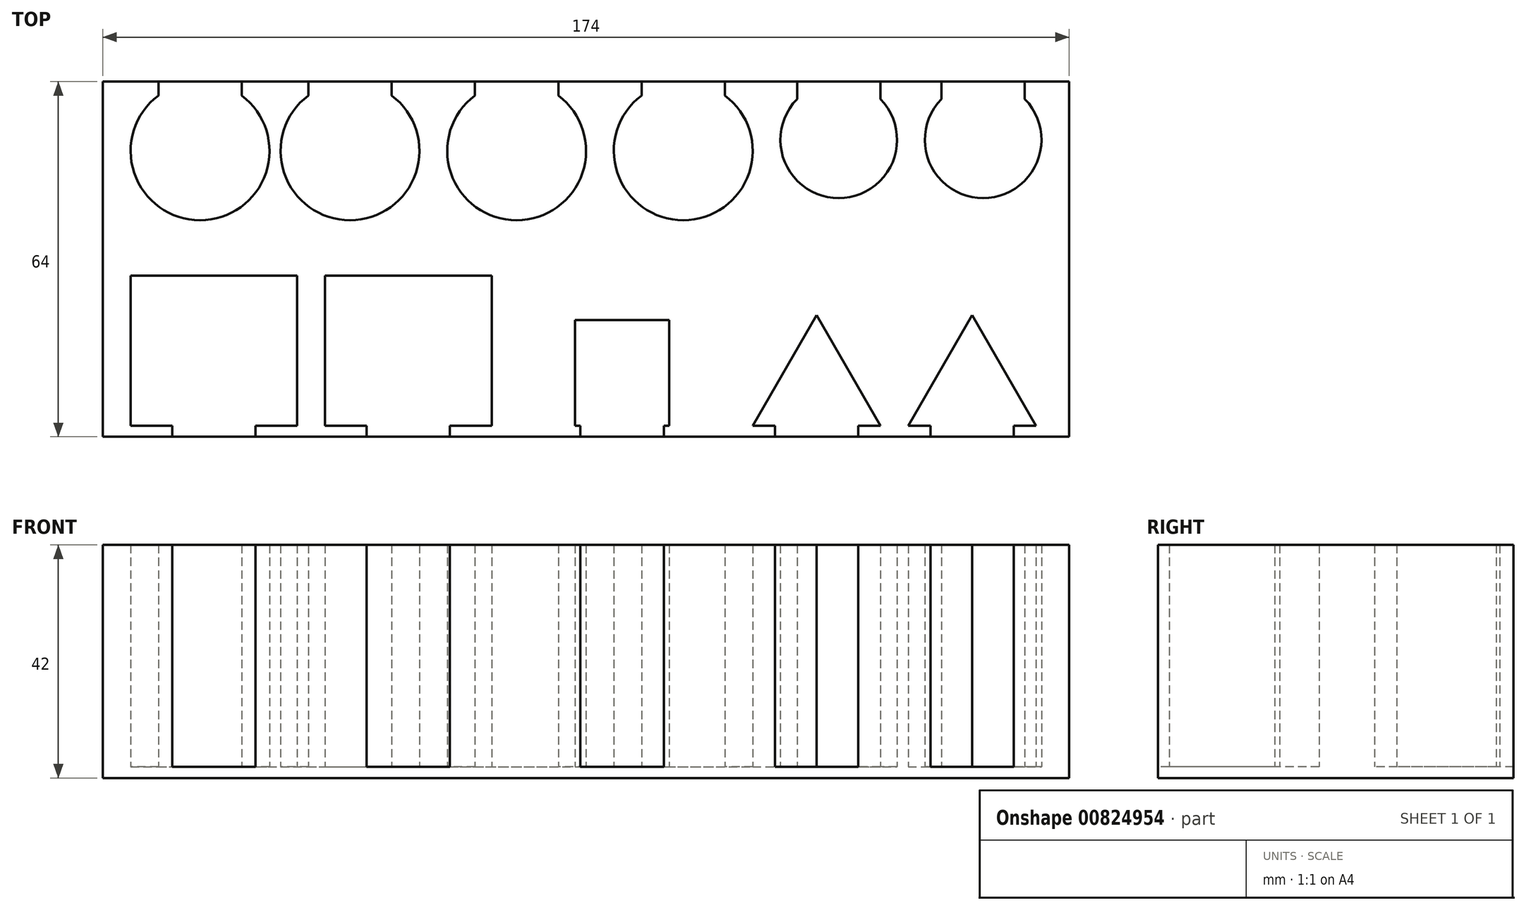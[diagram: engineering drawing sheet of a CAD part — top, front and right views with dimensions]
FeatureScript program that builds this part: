
annotation { "Feature Type Name" : "Feature", "Feature Type Description" : "" }
export const myFeature = defineFeature(function(context is Context, id is Id, definition is map)
    precondition{}
    {
        {
            var Q0;
            Q0=qCreatedBy(makeId("Top.planeOp"),FACE);
            var sketch = newSketch(context, id + "F0", { "sketchPlane" : qUnion([Q0])});
            skLineSegment(sketch, "E0.bottom", {"start": v(0, 0) * mm, "end": v(174, 0) * mm});
            skLineSegment(sketch, "E0.top", {"start": v(0, 64) * mm, "end": v(174, 64) * mm});
            skLineSegment(sketch, "E0.left", {"start": v(0, 0) * mm, "end": v(0, 64) * mm});
            skLineSegment(sketch, "E0.right", {"start": v(174, 0) * mm, "end": v(174, 64) * mm});
            skLineSegment(sketch, "E1.bottom", {"start": v(5, 29) * mm, "end": v(35, 29) * mm});
            skLineSegment(sketch, "E1.top", {"start": v(5, 2) * mm, "end": v(35, 2) * mm});
            skLineSegment(sketch, "E1.left", {"start": v(5, 29) * mm, "end": v(5, 2) * mm});
            skLineSegment(sketch, "E1.right", {"start": v(35, 29) * mm, "end": v(35, 2) * mm});
            skLineSegment(sketch, "E2.bottom", {"start": v(40, 29) * mm, "end": v(70, 29) * mm});
            skLineSegment(sketch, "E2.top", {"start": v(40, 2) * mm, "end": v(70, 2) * mm});
            skLineSegment(sketch, "E2.left", {"start": v(40, 29) * mm, "end": v(40, 2) * mm});
            skLineSegment(sketch, "E2.right", {"start": v(70, 29) * mm, "end": v(70, 2) * mm});
            skLineSegment(sketch, "E3.bottom", {"start": v(85, 21) * mm, "end": v(102, 21) * mm});
            skLineSegment(sketch, "E3.top", {"start": v(85, 2) * mm, "end": v(102, 2) * mm});
            skLineSegment(sketch, "E3.left", {"start": v(85, 21) * mm, "end": v(85, 2) * mm});
            skLineSegment(sketch, "E3.right", {"start": v(102, 21) * mm, "end": v(102, 2) * mm});
            skLineSegment(sketch, "E4", {"start": v(128.5, 21.92) * mm, "end": v(117, 2) * mm});
            skLineSegment(sketch, "E5", {"start": v(117, 2) * mm, "end": v(140, 2) * mm});
            skLineSegment(sketch, "E6", {"start": v(140, 2) * mm, "end": v(128.5, 21.92) * mm});
            skLineSegment(sketch, "E7", {"start": v(156.5, 21.92) * mm, "end": v(145, 2) * mm});
            skLineSegment(sketch, "E8", {"start": v(145, 2) * mm, "end": v(168, 2) * mm});
            skLineSegment(sketch, "E9", {"start": v(168, 2) * mm, "end": v(156.5, 21.92) * mm});
            skCircle(sketch, "E10", {"center": v(74.5, 51.5) * mm, "radius": 12.5 * mm});
            skCircle(sketch, "E11", {"center": v(104.5, 51.5) * mm, "radius": 12.5 * mm});
            skLineSegment(sketch, "E12", {"start": v(74.5, 51.5) * mm, "end": v(104.5, 51.5) * mm, "construction": true});
            skCircle(sketch, "E13", {"center": v(132.5, 53.5) * mm, "radius": 10.5 * mm});
            skCircle(sketch, "E14", {"center": v(158.5, 53.5) * mm, "radius": 10.5 * mm});
            skLineSegment(sketch, "E15", {"start": v(132.5, 53.5) * mm, "end": v(158.5, 53.5) * mm, "construction": true});
            skCircle(sketch, "E16", {"center": v(17.5, 51.5) * mm, "radius": 12.5 * mm});
            skCircle(sketch, "E17", {"center": v(44.5, 51.5) * mm, "radius": 12.5 * mm});
            skLineSegment(sketch, "E18", {"start": v(17.5, 51.5) * mm, "end": v(44.5, 51.5) * mm, "construction": true});
            skLineSegment(sketch, "E19.bottom", {"start": v(117, 51.5) * mm, "end": v(122, 51.5) * mm, "construction": true});
            skLineSegment(sketch, "E19.top", {"start": v(117, 41.5) * mm, "end": v(122, 41.5) * mm, "construction": true});
            skLineSegment(sketch, "E19.left", {"start": v(117, 51.5) * mm, "end": v(117, 41.5) * mm, "construction": true});
            skLineSegment(sketch, "E19.right", {"start": v(122, 51.5) * mm, "end": v(122, 41.5) * mm, "construction": true});
            skLineSegment(sketch, "E20.bottom", {"start": v(10, 64) * mm, "end": v(25, 64) * mm});
            skLineSegment(sketch, "E20.top", {"start": v(10, 51.5) * mm, "end": v(25, 51.5) * mm});
            skLineSegment(sketch, "E20.left", {"start": v(10, 64) * mm, "end": v(10, 51.5) * mm});
            skLineSegment(sketch, "E20.right", {"start": v(25, 64) * mm, "end": v(25, 51.5) * mm});
            skLineSegment(sketch, "E21.bottom", {"start": v(37, 64) * mm, "end": v(52, 64) * mm});
            skLineSegment(sketch, "E21.top", {"start": v(37, 51.5) * mm, "end": v(52, 51.5) * mm});
            skLineSegment(sketch, "E21.left", {"start": v(37, 64) * mm, "end": v(37, 51.5) * mm});
            skLineSegment(sketch, "E21.right", {"start": v(52, 64) * mm, "end": v(52, 51.5) * mm});
            skLineSegment(sketch, "E22.bottom", {"start": v(67, 64) * mm, "end": v(82, 64) * mm});
            skLineSegment(sketch, "E22.top", {"start": v(67, 51.5) * mm, "end": v(82, 51.5) * mm});
            skLineSegment(sketch, "E22.left", {"start": v(67, 64) * mm, "end": v(67, 51.5) * mm});
            skLineSegment(sketch, "E22.right", {"start": v(82, 64) * mm, "end": v(82, 51.5) * mm});
            skLineSegment(sketch, "E23.bottom", {"start": v(97, 64) * mm, "end": v(112, 64) * mm});
            skLineSegment(sketch, "E23.top", {"start": v(97, 51.5) * mm, "end": v(112, 51.5) * mm});
            skLineSegment(sketch, "E23.left", {"start": v(97, 64) * mm, "end": v(97, 51.5) * mm});
            skLineSegment(sketch, "E23.right", {"start": v(112, 64) * mm, "end": v(112, 51.5) * mm});
            skLineSegment(sketch, "E24.bottom", {"start": v(125, 64) * mm, "end": v(140, 64) * mm});
            skLineSegment(sketch, "E24.top", {"start": v(125, 53.5) * mm, "end": v(140, 53.5) * mm});
            skLineSegment(sketch, "E24.left", {"start": v(125, 64) * mm, "end": v(125, 53.5) * mm});
            skLineSegment(sketch, "E24.right", {"start": v(140, 64) * mm, "end": v(140, 53.5) * mm});
            skLineSegment(sketch, "E25.bottom", {"start": v(151, 64) * mm, "end": v(166, 64) * mm});
            skLineSegment(sketch, "E25.top", {"start": v(151, 53.5) * mm, "end": v(166, 53.5) * mm});
            skLineSegment(sketch, "E25.left", {"start": v(151, 64) * mm, "end": v(151, 53.5) * mm});
            skLineSegment(sketch, "E25.right", {"start": v(166, 64) * mm, "end": v(166, 53.5) * mm});
            skLineSegment(sketch, "E26.bottom", {"start": v(121, 8.93) * mm, "end": v(136, 8.93) * mm});
            skLineSegment(sketch, "E26.top", {"start": v(121, 0) * mm, "end": v(136, 0) * mm});
            skLineSegment(sketch, "E26.left", {"start": v(121, 8.93) * mm, "end": v(121, 0) * mm});
            skLineSegment(sketch, "E26.right", {"start": v(136, 8.93) * mm, "end": v(136, 0) * mm});
            skLineSegment(sketch, "E27.bottom", {"start": v(149, 8.93) * mm, "end": v(164, 8.93) * mm});
            skLineSegment(sketch, "E27.top", {"start": v(149, 0) * mm, "end": v(164, 0) * mm});
            skLineSegment(sketch, "E27.left", {"start": v(149, 8.93) * mm, "end": v(149, 0) * mm});
            skLineSegment(sketch, "E27.right", {"start": v(164, 8.93) * mm, "end": v(164, 0) * mm});
            skLineSegment(sketch, "E28.bottom", {"start": v(86, 2) * mm, "end": v(101, 2) * mm});
            skLineSegment(sketch, "E28.top", {"start": v(86, 0) * mm, "end": v(101, 0) * mm});
            skLineSegment(sketch, "E28.left", {"start": v(86, 2) * mm, "end": v(86, 0) * mm});
            skLineSegment(sketch, "E28.right", {"start": v(101, 2) * mm, "end": v(101, 0) * mm});
            skPoint(sketch, "E29", {"position": v(93.5, 2) * mm});
            skPoint(sketch, "E30", {"position": v(55, 2) * mm});
            skPoint(sketch, "E31", {"position": v(20, 2) * mm});
            skLineSegment(sketch, "E32.bottom", {"start": v(12.5, 2) * mm, "end": v(27.5, 2) * mm});
            skLineSegment(sketch, "E32.top", {"start": v(12.5, 0) * mm, "end": v(27.5, 0) * mm});
            skLineSegment(sketch, "E32.left", {"start": v(12.5, 2) * mm, "end": v(12.5, 0) * mm});
            skLineSegment(sketch, "E32.right", {"start": v(27.5, 2) * mm, "end": v(27.5, 0) * mm});
            skLineSegment(sketch, "E33.bottom", {"start": v(47.5, 2) * mm, "end": v(62.5, 2) * mm});
            skLineSegment(sketch, "E33.top", {"start": v(47.5, 0) * mm, "end": v(62.5, 0) * mm});
            skLineSegment(sketch, "E33.left", {"start": v(47.5, 2) * mm, "end": v(47.5, 0) * mm});
            skLineSegment(sketch, "E33.right", {"start": v(62.5, 2) * mm, "end": v(62.5, 0) * mm});
            skSolve(sketch);
        }
        {
            var Q0;
            Q0=makeQuery(id+"F0.imprint","IMPRINT",FACE,{"disambiguationData":[TD([[makeQuery(id+"F0.imprint","IMPRINT",EDGE,{"derivedFrom":sQuery(id+"F0.wireOp",EDGE,"E0.bottom")}),1.0]])]});
            extrude(context, id + "F1", {"entities" : qUnion([Q0]), "depth" : 40 * mm, "offsetDistance" : 25 * mm});
        }
        {
            var Q0;
            Q0=makeQuery(id+"F1.opExtrude","CAP_FACE",FACE,{"disambiguationData":[OSD([sQuery(id+"F0.wireOp",EDGE,"E0.bottom"),sQuery(id+"F0.wireOp",EDGE,"E0.top"),sQuery(id+"F0.wireOp",EDGE,"E0.left"),sQuery(id+"F0.wireOp",EDGE,"E0.right"),sQuery(id+"F0.wireOp",EDGE,"E1.bottom"),sQuery(id+"F0.wireOp",EDGE,"E1.top"),sQuery(id+"F0.wireOp",EDGE,"E1.left"),sQuery(id+"F0.wireOp",EDGE,"E1.right"),sQuery(id+"F0.wireOp",EDGE,"E2.bottom"),sQuery(id+"F0.wireOp",EDGE,"E2.top"),sQuery(id+"F0.wireOp",EDGE,"E2.left"),sQuery(id+"F0.wireOp",EDGE,"E2.right"),sQuery(id+"F0.wireOp",EDGE,"E3.bottom"),sQuery(id+"F0.wireOp",EDGE,"E3.top"),sQuery(id+"F0.wireOp",EDGE,"E3.left"),sQuery(id+"F0.wireOp",EDGE,"E3.right"),sQuery(id+"F0.wireOp",EDGE,"E4"),sQuery(id+"F0.wireOp",EDGE,"E5"),sQuery(id+"F0.wireOp",EDGE,"E6"),sQuery(id+"F0.wireOp",EDGE,"E7"),sQuery(id+"F0.wireOp",EDGE,"E8"),sQuery(id+"F0.wireOp",EDGE,"E9"),sQuery(id+"F0.wireOp",EDGE,"E10"),sQuery(id+"F0.wireOp",EDGE,"E11"),sQuery(id+"F0.wireOp",EDGE,"E13"),sQuery(id+"F0.wireOp",EDGE,"E14"),sQuery(id+"F0.wireOp",EDGE,"E16"),sQuery(id+"F0.wireOp",EDGE,"E17"),sQuery(id+"F0.wireOp",EDGE,"E20.left"),sQuery(id+"F0.wireOp",EDGE,"E20.right"),sQuery(id+"F0.wireOp",EDGE,"E21.left"),sQuery(id+"F0.wireOp",EDGE,"E21.right"),sQuery(id+"F0.wireOp",EDGE,"E22.left"),sQuery(id+"F0.wireOp",EDGE,"E22.right"),sQuery(id+"F0.wireOp",EDGE,"E23.left"),sQuery(id+"F0.wireOp",EDGE,"E23.right"),sQuery(id+"F0.wireOp",EDGE,"E24.left"),sQuery(id+"F0.wireOp",EDGE,"E24.right"),sQuery(id+"F0.wireOp",EDGE,"E25.left"),sQuery(id+"F0.wireOp",EDGE,"E25.right"),sQuery(id+"F0.wireOp",EDGE,"E26.left"),sQuery(id+"F0.wireOp",EDGE,"E26.right"),sQuery(id+"F0.wireOp",EDGE,"E27.left"),sQuery(id+"F0.wireOp",EDGE,"E27.right"),sQuery(id+"F0.wireOp",EDGE,"E28.left"),sQuery(id+"F0.wireOp",EDGE,"E28.right"),sQuery(id+"F0.wireOp",EDGE,"E32.left"),sQuery(id+"F0.wireOp",EDGE,"E32.right"),sQuery(id+"F0.wireOp",EDGE,"E33.left"),sQuery(id+"F0.wireOp",EDGE,"E33.right")])],"isStart":true});
            var sketch = newSketch(context, id + "F2", { "sketchPlane" : qUnion([Q0])});
            skLineSegment(sketch, "E34.bottom", {"start": v(0, -64) * mm, "end": v(174, -64) * mm});
            skLineSegment(sketch, "E34.top", {"start": v(0, 0) * mm, "end": v(174, 0) * mm});
            skLineSegment(sketch, "E34.left", {"start": v(0, -64) * mm, "end": v(0, 0) * mm});
            skLineSegment(sketch, "E34.right", {"start": v(174, -64) * mm, "end": v(174, 0) * mm});
            skSolve(sketch);
        }
        {
            var Q0;
            Q0 = qSketchRegion(id + "F2", true);
            extrude(context, id + "F3", {"entities" : qUnion([Q0]), "operationType" : NewBodyOperationType.ADD, "depth" : 2 * mm, "offsetDistance" : 25 * mm});
        }
    });
